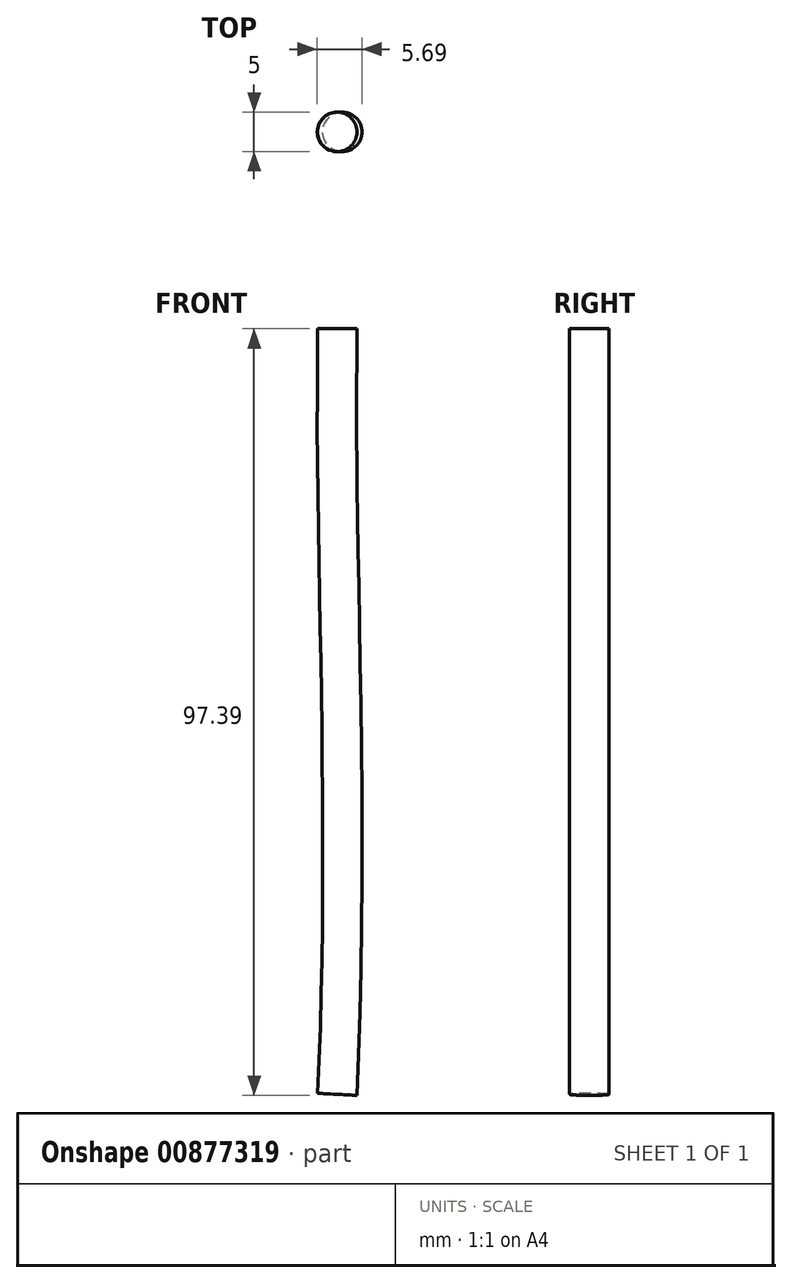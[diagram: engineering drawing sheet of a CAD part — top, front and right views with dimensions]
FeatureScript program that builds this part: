
annotation { "Feature Type Name" : "Feature", "Feature Type Description" : "" }
export const myFeature = defineFeature(function(context is Context, id is Id, definition is map)
    precondition{}
    {
        {
            var Q0;
            Q0=qCreatedBy(makeId("Top.planeOp"),FACE);
            var sketch = newSketch(context, id + "F0", { "sketchPlane" : qUnion([Q0])});
            skCircle(sketch, "E0", {"center": v(0, 0) * mm, "radius": 2.5 * mm});
            skSolve(sketch);
        }
        {
            var Q0;
            Q0=qCreatedBy(makeId("Front.planeOp"),FACE);
            var sketch = newSketch(context, id + "F1", { "sketchPlane" : qUnion([Q0])});
            skFitSpline(sketch, "E1", {"points": [v(0, 0) * mm, v(0, -18.72) * mm, v(0, -97.26) * mm], "startDerivative": vector(0, -55.45) * mm, "endDerivative": vector(-5.94, -115.54) * mm});
            skSolve(sketch);
        }
        {
            var Q0;
            Q0=qSketchRegion(id+"F0",true);
            var Q1;
            Q1=sQuery(id+"F1.wireOp",EDGE,"E1");
            sweep(context, id + "F2", {"profiles" : qUnion([Q0]), "path" : qUnion([Q1])});
        }
    });
